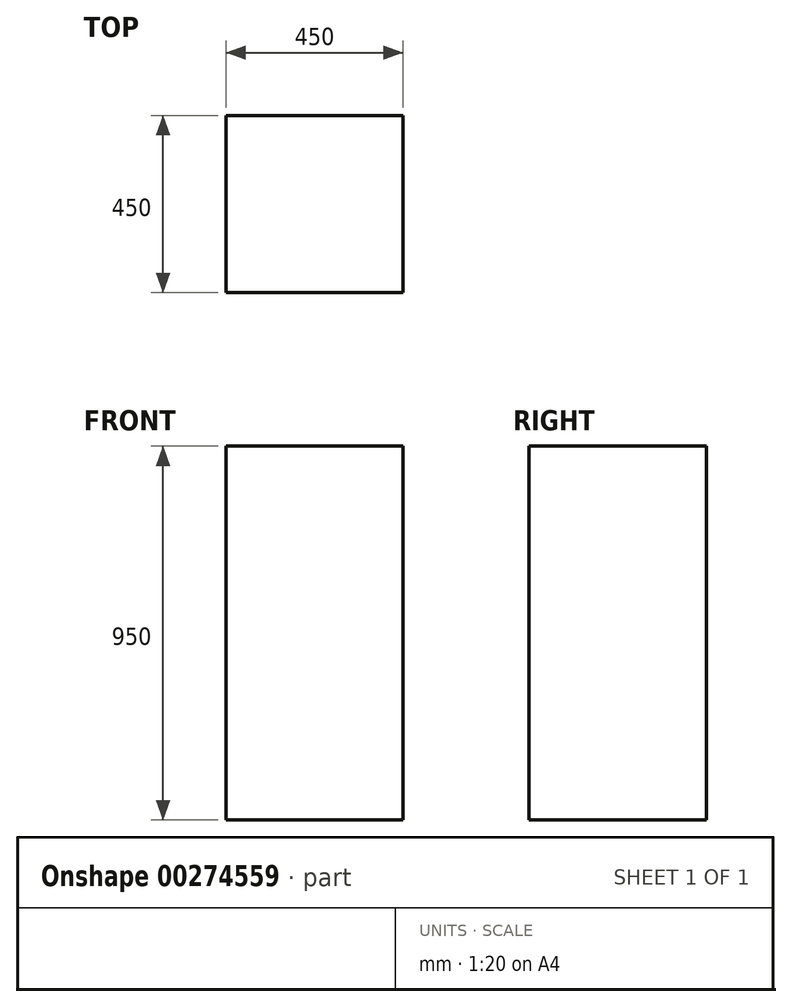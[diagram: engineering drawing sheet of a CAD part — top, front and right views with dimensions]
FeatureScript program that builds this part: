
annotation { "Feature Type Name" : "Feature", "Feature Type Description" : "" }
export const myFeature = defineFeature(function(context is Context, id is Id, definition is map)
    precondition{}
    {
        {
            var Q0;
            Q0=qCreatedBy(makeId("Top.planeOp"),FACE);
            var sketch = newSketch(context, id + "F0", { "sketchPlane" : qUnion([Q0])});
            skLineSegment(sketch, "E0.bottom", {"start": v(225, 225) * mm, "end": v(-225, 225) * mm});
            skLineSegment(sketch, "E0.top", {"start": v(225, -225) * mm, "end": v(-225, -225) * mm});
            skLineSegment(sketch, "E0.left", {"start": v(225, 225) * mm, "end": v(225, -225) * mm});
            skLineSegment(sketch, "E0.right", {"start": v(-225, 225) * mm, "end": v(-225, -225) * mm});
            skPoint(sketch, "E0.middle", {"position": v(0, 0) * mm});
            skSolve(sketch);
        }
        {
            var Q0;
            Q0=qSketchRegion(id+"F0",true);
            extrude(context, id + "F1", {"entities" : qUnion([Q0]), "depth" : 950 * mm});
        }
    });
